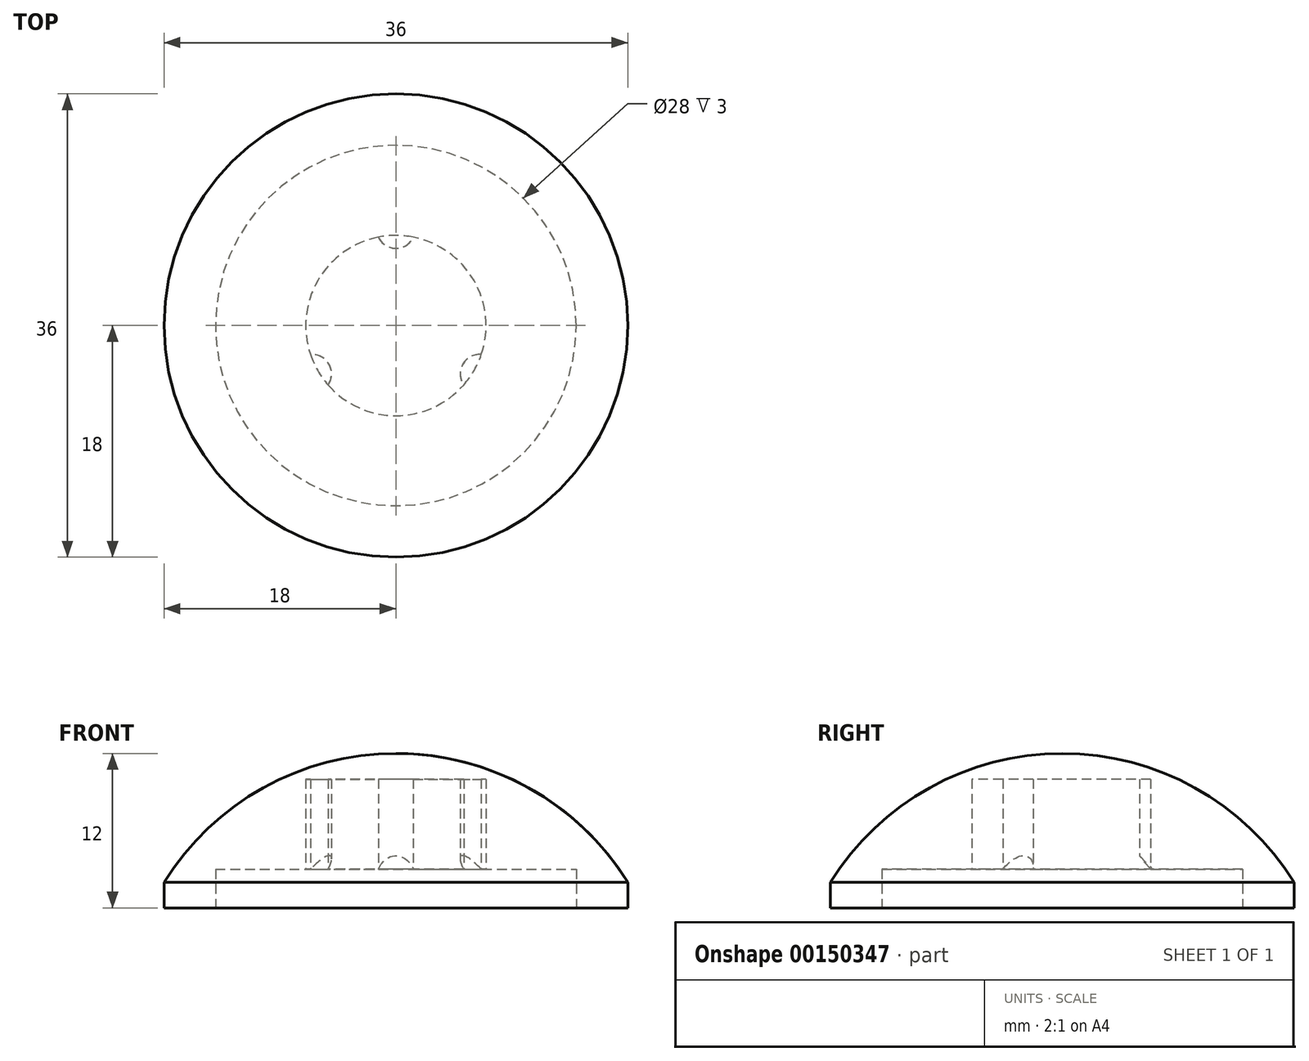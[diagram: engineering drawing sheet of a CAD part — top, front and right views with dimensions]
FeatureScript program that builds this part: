
annotation { "Feature Type Name" : "Feature", "Feature Type Description" : "" }
export const myFeature = defineFeature(function(context is Context, id is Id, definition is map)
    precondition{}
    {
        {
            var Q0;
            Q0=qCreatedBy(makeId("Front.planeOp"),FACE);
            var sketch = newSketch(context, id + "F0", { "sketchPlane" : qUnion([Q0])});
            skLineSegment(sketch, "E0", {"start": v(0, 0) * mm, "end": v(0, 14.56) * mm, "construction": true});
            skLineSegment(sketch, "E1", {"start": v(0, 10) * mm, "end": v(7, 10) * mm});
            skLineSegment(sketch, "E2", {"start": v(7, 10) * mm, "end": v(7, 3) * mm});
            skLineSegment(sketch, "E3", {"start": v(7, 3) * mm, "end": v(14, 3) * mm});
            skLineSegment(sketch, "E4", {"start": v(14, 3) * mm, "end": v(14, 0) * mm});
            skLineSegment(sketch, "E5", {"start": v(14, 0) * mm, "end": v(18, 0) * mm});
            skLineSegment(sketch, "E6", {"start": v(18, 0) * mm, "end": v(18, 2) * mm});
            skArc(sketch, "E7", {"start": v(18, 2) * mm, "mid": v(10.3, 9.33) * mm, "end": v(0, 12) * mm});
            skLineSegment(sketch, "E8", {"start": v(0, 12) * mm, "end": v(-16.74, 12) * mm, "construction": true});
            skLineSegment(sketch, "E9", {"start": v(0, 10) * mm, "end": v(0, 12) * mm});
            skLineSegment(sketch, "E10", {"start": v(7, 3) * mm, "end": v(5.15, 4.96) * mm});
            skLineSegment(sketch, "E11", {"start": v(5.15, 4.96) * mm, "end": v(4.5, 1.26) * mm});
            skLineSegment(sketch, "E12", {"start": v(4.5, 1.26) * mm, "end": v(7, 3) * mm});
            skSolve(sketch);
        }
        {
            var Q0;
            Q0=makeQuery(id+"F0.imprint","IMPRINT",FACE,{"disambiguationData":[TD([[makeQuery(id+"F0.imprint","IMPRINT",EDGE,{"derivedFrom":sQuery(id+"F0.wireOp",EDGE,"E1")}),1.0]])]});
            var Q1;
            Q1=sQuery(id+"F0.wireOp",EDGE,"E0");
            revolve(context, id + "F1", {"surfaceOperationType" : NewSurfaceOperationType.NEW, "entities" : qUnion([Q0]), "axis" : qUnion([Q1]), "revolveType" : RevolveType.FULL});
        }
        {
            var Q0;
            Q0=makeQuery(id+"F1.opRevolve","SWEPT_FACE",FACE,{"disambiguationData":[OSD([sQuery(id+"F0.wireOp",EDGE,"E3")])]});
            var sketch = newSketch(context, id + "F2", { "sketchPlane" : qUnion([Q0])});
            skLineSegment(sketch, "E13", {"start": v(0, 0) * mm, "end": v(0, -7) * mm, "construction": true});
            skArc(sketch, "E14", {"start": v(1.36, -6.87) * mm, "mid": v(0, -6) * mm, "end": v(-1.36, -6.87) * mm});
            skPoint(sketch, "E15.center", {"position": v(0, 0) * mm});
            skArc(sketch, "E16.0", {"start": v(-1.36, -6.87) * mm, "mid": v(0, -7) * mm, "end": v(1.36, -6.87) * mm});
            skSolve(sketch);
        }
        {
            var Q0;
            Q0 = qSketchRegion(id + "F2", true);
            var Q1;
            Q1=makeQuery(id+"F1.opRevolve","SWEPT_FACE",FACE,{"disambiguationData":[OSD([sQuery(id+"F0.wireOp",EDGE,"E1")])]});
            extrude(context, id + "F3", {"entities" : qUnion([Q0]), "operationType" : NewBodyOperationType.ADD, "endBound" : BoundingType.UP_TO_SURFACE, "oppositeDirection" : true, "depth" : 25 * mm, "endBoundEntityFace" : qUnion([Q1]), "offsetDistance" : 25 * mm});
        }
        {
            var Q0;
            Q0=makeQuery(id+"F1.opRevolve","SWEPT_BODY",BODY,{"disambiguationData":[OSD([sQuery(id+"F0.wireOp",EDGE,"E1"),sQuery(id+"F0.wireOp",EDGE,"E2"),sQuery(id+"F0.wireOp",EDGE,"E3"),sQuery(id+"F0.wireOp",EDGE,"E4"),sQuery(id+"F0.wireOp",EDGE,"E5"),sQuery(id+"F0.wireOp",EDGE,"E6"),sQuery(id+"F0.wireOp",EDGE,"E7"),sQuery(id+"F0.wireOp",EDGE,"E9")])]});
            var Q1;
            Q1=makeQuery(id+"F1.opRevolve","SWEPT_FACE",FACE,{"disambiguationData":[OSD([sQuery(id+"F0.wireOp",EDGE,"E2")])]});
            circularPattern(context, id + "F4", {"operationType" : NewBodyOperationType.ADD, "entities" : qUnion([Q0]), "axis" : qUnion([Q1]), "angle" : 360 * degree, "instanceCount" : 3, "equalSpace" : true});
        }
        {
            var Q0;
            Q0=makeQuery(id+"F0.imprint","IMPRINT",FACE,{"disambiguationData":[TD([[makeQuery(id+"F0.imprint","IMPRINT",EDGE,{"derivedFrom":sQuery(id+"F0.wireOp",EDGE,"E10")}),1.0]])]});
            var Q1;
            {var subQ0=sQuery(id+"F2.wireOp",EDGE,"E14");var subQ1=makeQuery(id+"F3.opExtrude","CAP_FACE",FACE,{"disambiguationData":[OSD([subQ0,sQuery(id+"F2.wireOp",EDGE,"E16.0")])],"isStart":true});var subQ2=makeQuery(id+"F1.opRevolve","SWEPT_FACE",FACE,{"disambiguationData":[OSD([sQuery(id+"F0.wireOp",EDGE,"E3")])]});var subQ3=makeQuery(id+"F3.opExtrude","SWEPT_FACE",FACE,{"disambiguationData":[OSD([subQ0])]});var subQ4=makeQuery(id+"F3.boolean.opBoolean","MERGE",FACE,{"derivedFrom":[subQ2,subQ1]});Q1=makeQuery(id+"F4.boolean.opBoolean","SPLIT",FACE,{"disambiguationData":[TD([makeQuery(id+"F1.opRevolve","SWEPT_FACE",FACE,{"disambiguationData":[OSD([sQuery(id+"F0.wireOp",EDGE,"E1")])]}),subQ2,subQ3,subQ1,makeQuery(id+"F4.opPattern","COPY",FACE,{"derivedFrom":subQ4,"instanceName":"1"}),makeQuery(id+"F4.opPattern","COPY",FACE,{"derivedFrom":subQ3,"instanceName":"2"}),makeQuery(id+"F4.opPattern","COPY",FACE,{"derivedFrom":subQ4,"instanceName":"2"})])],"derivedFrom":makeQuery(id+"F1.opRevolve","SWEPT_FACE",FACE,{"disambiguationData":[OSD([sQuery(id+"F0.wireOp",EDGE,"E2")])]})});}
            revolve(context, id + "F5", {"operationType" : NewBodyOperationType.REMOVE, "surfaceOperationType" : NewSurfaceOperationType.NEW, "entities" : qUnion([Q0]), "axis" : qUnion([Q1]), "revolveType" : RevolveType.FULL, "oppositeDirection" : true});
        }
    });
